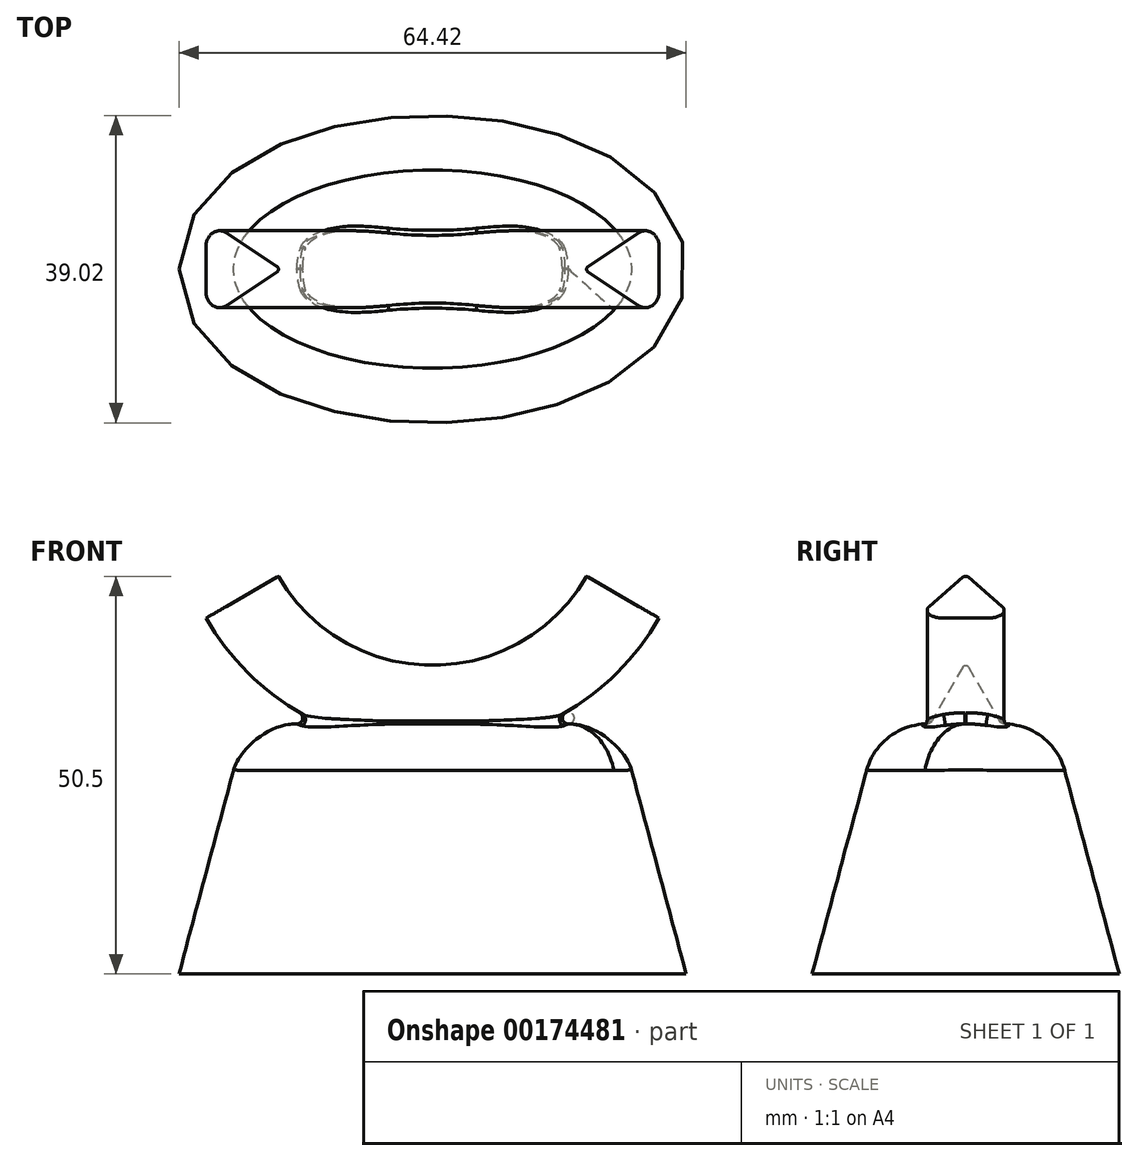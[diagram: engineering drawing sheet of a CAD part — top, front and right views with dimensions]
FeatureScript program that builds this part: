
annotation { "Feature Type Name" : "Feature", "Feature Type Description" : "" }
export const myFeature = defineFeature(function(context is Context, id is Id, definition is map)
    precondition{}
    {
        {
            var Q0;
            Q0=qCreatedBy(makeId("Right.planeOp"),FACE);
            var sketch = newSketch(context, id + "F0", { "sketchPlane" : qUnion([Q0])});
            skLineSegment(sketch, "E0", {"start": v(-6.35, 3.18) * mm, "end": v(0, 14.17) * mm});
            skLineSegment(sketch, "E1", {"start": v(0, 14.17) * mm, "end": v(6.35, 3.18) * mm});
            skLineSegment(sketch, "E2", {"start": v(6.35, 3.17) * mm, "end": v(-6.35, 3.18) * mm});
            skLineSegment(sketch, "E3", {"start": v(-8.44, 36.4) * mm, "end": v(15.4, 36.4) * mm, "construction": true});
            skSolve(sketch);
        }
        {
            var Q0;
            Q0=makeQuery(id+"F0.imprint","IMPRINT",FACE,{"disambiguationData":[TD([[makeQuery(id+"F0.imprint","IMPRINT",EDGE,{"derivedFrom":sQuery(id+"F0.wireOp",EDGE,"E0")}),-1.0]])]});
            var Q1;
            Q1=sQuery(id+"F0.wireOp",EDGE,"E3");
            revolve(context, id + "F1", {"entities" : qUnion([Q0]), "axis" : qUnion([Q1]), "revolveType" : RevolveType.SYMMETRIC, "angle" : 120 * degree});
        }
        {
            var Q0;
            Q0=qCreatedBy(makeId("Top.planeOp"),FACE);
            var sketch = newSketch(context, id + "F2", { "sketchPlane" : qUnion([Q0])});
            skEllipse(sketch, "E4", {"center": v(0, 0) * mm, "majorRadius": 25.4 * mm, "minorRadius": 12.7 * mm, "majorAxis": v(1, 0)});
            skSolve(sketch);
        }
        {
            var Q0;
            Q0 = qSketchRegion(id + "F2", true);
            extrude(context, id + "F3", {"entities" : qUnion([Q0]), "operationType" : NewBodyOperationType.ADD, "depth" : 6.35 * mm, "hasDraft" : true, "draftAngle" : 15 * degree, "draftPullDirection" : true, "hasSecondDirection" : true, "secondDirectionOppositeDirection" : true, "secondDirectionDepth" : 25.4 * mm, "hasSecondDirectionDraft" : true, "secondDirectionDraftAngle" : 15 * degree});
        }
        {
            var Q0;
            Q0=makeQuery(id+"F3.opExtrude","CAP_EDGE",EDGE,{"disambiguationData":[OSD([sQuery(id+"F2.wireOp",EDGE,"E4")])],"isStart":false});
            fillet(context, id + "F4", {"entities" : qUnion([Q0]), "radius" : 8 * mm, "tangentPropagation" : true, "allowEdgeOverflow" : false});
        }
        {
            var Q0;
            {var subQ0=sQuery(id+"F0.wireOp",EDGE,"E0");var subQ1=sQuery(id+"F0.wireOp",EDGE,"E2");Q0=makeQuery(id+"F3.boolean.opBoolean","SPLIT",EDGE,{"disambiguationData":[TD([makeQuery(id+"F1.opRevolve","CAP_FACE",FACE,{"disambiguationData":[OSD([subQ0,sQuery(id+"F0.wireOp",EDGE,"E1"),subQ1])],"isStart":false})])],"derivedFrom":makeQuery(id+"F1.opRevolve","SWEPT_EDGE",EDGE,{"disambiguationData":[OSD([subQ0,subQ1])]})});}
            var Q1;
            {var subQ0=sQuery(id+"F0.wireOp",EDGE,"E2");var subQ1=sQuery(id+"F0.wireOp",EDGE,"E1");Q1=makeQuery(id+"F3.boolean.opBoolean","SPLIT",EDGE,{"disambiguationData":[TD([makeQuery(id+"F1.opRevolve","CAP_FACE",FACE,{"disambiguationData":[OSD([sQuery(id+"F0.wireOp",EDGE,"E0"),subQ1,subQ0])],"isStart":false})])],"derivedFrom":makeQuery(id+"F1.opRevolve","SWEPT_EDGE",EDGE,{"disambiguationData":[OSD([subQ1,subQ0])]})});}
            var Q2;
            {var subQ0=sQuery(id+"F0.wireOp",EDGE,"E0");var subQ1=sQuery(id+"F0.wireOp",EDGE,"E2");Q2=makeQuery(id+"F3.boolean.opBoolean","SPLIT",EDGE,{"disambiguationData":[TD([makeQuery(id+"F1.opRevolve","CAP_FACE",FACE,{"disambiguationData":[OSD([subQ0,sQuery(id+"F0.wireOp",EDGE,"E1"),subQ1])],"isStart":true})])],"derivedFrom":makeQuery(id+"F1.opRevolve","SWEPT_EDGE",EDGE,{"disambiguationData":[OSD([subQ0,subQ1])]})});}
            var Q3;
            {var subQ0=sQuery(id+"F0.wireOp",EDGE,"E2");var subQ1=sQuery(id+"F0.wireOp",EDGE,"E1");Q3=makeQuery(id+"F3.boolean.opBoolean","SPLIT",EDGE,{"disambiguationData":[TD([makeQuery(id+"F1.opRevolve","CAP_FACE",FACE,{"disambiguationData":[OSD([sQuery(id+"F0.wireOp",EDGE,"E0"),subQ1,subQ0])],"isStart":true})])],"derivedFrom":makeQuery(id+"F1.opRevolve","SWEPT_EDGE",EDGE,{"disambiguationData":[OSD([subQ1,subQ0])]})});}
            fillet(context, id + "F5", {"entities" : qUnion([Q0, Q1, Q2, Q3]), "radius" : 2 * mm, "tangentPropagation" : true, "allowEdgeOverflow" : false});
        }
        {
            var Q0;
            Q0=makeQuery(id+"F3.boolean.opBoolean","INTERSECT",EDGE,{"disambiguationData":[OD(0.0)],"derivedFrom":[makeQuery(id+"F1.opRevolve","SWEPT_FACE",FACE,{"disambiguationData":[OSD([sQuery(id+"F0.wireOp",EDGE,"E2")])]}),makeQuery(id+"F3.opExtrude","CAP_FACE",FACE,{"disambiguationData":[OSD([sQuery(id+"F2.wireOp",EDGE,"E4")])],"isStart":false})]});
            fillet(context, id + "F6", {"entities" : qUnion([Q0]), "radius" : 0.76 * mm, "tangentPropagation" : true, "allowEdgeOverflow" : false});
        }
        {
            var Q0;
            Q0=makeQuery(id+"F1.opRevolve","SWEPT_EDGE",EDGE,{"disambiguationData":[OSD([sQuery(id+"F0.wireOp",EDGE,"E0"),sQuery(id+"F0.wireOp",EDGE,"E1")])]});
            fillet(context, id + "F7", {"entities" : qUnion([Q0]), "radius" : 0.38 * mm, "tangentPropagation" : true, "allowEdgeOverflow" : false});
        }
    });
